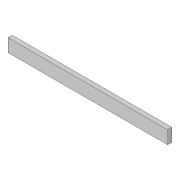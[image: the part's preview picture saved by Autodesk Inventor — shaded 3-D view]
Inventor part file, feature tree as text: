
AUTODESK INVENTOR PART (.ipt)
format: ipt  version: 2018 (Build 220112000, 112)  size: 75,264 bytes
history: native  units: in
note: dims shown in document units (in); Inventor stores cm internally (conversion verified against a paired STEP export)
features: extrude x1, sketch x1
ambient origin geometry x8: Origin, YZ Plane, XZ Plane, XY Plane, X Axis, Y Axis, Z Axis, Center Point
bodies: Solid1 (feature_tree)
feature tree (2):
  extrude  "Extrusion1"  TaperAngle=90.0deg  [1 undecoded]
  sketch  "Sketch1"  dims[d0=0.5906in d1=90.0deg d2=7.2835in d3=90.0deg d4=0.5906in d5=90.0deg d6=0.1969in d7=0.0in]
note: 1 required parameter value undecoded (feature->parameter linkage not recoverable at this tier; creation-order binding heuristic only, values carry confidence <= 0.55)
